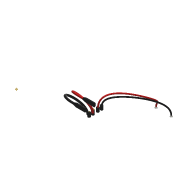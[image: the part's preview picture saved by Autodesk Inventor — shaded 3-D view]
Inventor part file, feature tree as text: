
AUTODESK INVENTOR PART (.ipt)
format: ipt  version: 2020 (Build 240168000, 168)  size: 544,256 bytes
history: native  units: in
note: dims shown in document units (in); Inventor stores cm internally (conversion verified against a paired STEP export)
features: other x18, reference x14, sketch x13, plane x10, sweep x6, pattern_linear x5, extrude x4, projected_geometry x4, loft x3
ambient origin geometry x8: Origin, YZ Plane, XZ Plane, XY Plane, X Axis, Y Axis, Z Axis, Center Point
bodies: Solid1 (feature_tree), Solid2 (feature_tree), Solid6 (feature_tree), Solid10 (feature_tree)
feature tree (77):
  sketch  "3D Sketch1"
  plane  "Work Plane1"
  extrude  "Extrusion1"  Depth=0.15in
  plane  "Work Plane2"
  loft  "Loft1"
  loft  "Loft2"
  sketch  "Sketch5"  dims[d11=0.06in d12=0.0in d13=90.0deg]
  sweep  "Sweep1"
  sweep  "Sweep2"
  plane  "Work Plane3"
  extrude  "Extrusion2"  Depth=0.05in
  plane  "Work Plane4"
  plane  "Work Plane5"
  sketch  "Sketch7"  dims[d18=0.0in d19=90.0deg d20=0.05in]
  plane  "Work Plane7"
  loft  "Loft3"
  pattern_linear  "Rectangular Pattern1"  Spacing1=0.1in  [1 undecoded]
  sketch  "Sketch9"  dims[d24=0.3937in d25=0.3937in]
  sweep  "Sweep3"
  sweep  "Sweep4"
  sketch  "3D Sketch2"
  plane  "Work Plane8"
  extrude  "Extrusion4"  Depth=0.03in
  plane  "Work Plane9"
  pattern_linear  "Rectangular Pattern3"  Spacing1=0.3937in  [1 undecoded]
  sketch  "Sketch13"  dims[d28=0.0in d29=0.0in]
  sweep  "Sweep6"
  sweep  "Sweep7"
  pattern_linear  "Rectangular Pattern4"  Spacing1=0.3937in  [1 undecoded]
  pattern_linear  "Rectangular Pattern5"  Count1=2 Spacing1=0.4in
  sketch  "Sketch14"  dims[d30=0.005in d31=0.1in d32=0.0in d37=0.175in d38=0.125in d39=0.03in d42=0.3937in d43=0.3937in d44=0.3937in d45=0.3937in d48=0.0in d49=90.0deg d50=0.3937in d51=90.0deg d52=0.7874in d54=0.4in d55=0.0in d56=0.0in d57=0.0in d58=0.0in d59=0.075in d60=0.07in d61=0.3937in d62=0.3937in d63=0.055in d64=0.03in d65=0.0in d75=6.2992in d77=0.1in d78=0.07in d79=0.05in d80=0.05in d81=0.0in d82=0.0in d83=0.0in d84=0.0in d85=0.7874in d87=1.5in d88=5.9055in d90=0.1in d91=0.025in d92=1.0in d93=0.0in d94=6.2992in d96=0.1in d97=0.0236in d98=0.0118in d100=0.0118in d101=0.0475in d102=0.0238in]
  plane  "Work Plane10"
  extrude  "Extrusion6"  TaperAngle=0.0deg  [1 undecoded]
  pattern_linear  "Rectangular Pattern6"  Spacing1=0.0in  [1 undecoded]
  other  "Work Point1"
  other  "Work Point2"
  other  "Work Point3"
  sketch  "Sketch1"  dims[d4=0.2in d5=0.15in]
  sketch  "Sketch2"  dims[d6=0.055in d7=0.0475in]
  other  "Edges1"
  sketch  "Sketch4"  dims[d8=0.2in d9=0.0in d10=0.0625in]
  other  "Edges2"
  projected_geometry  "Projected Loop1"
  projected_geometry  "Projected Loop2"
  sketch  "Sketch6"  dims[d14=0.0in d15=90.0deg d16=0.0in d17=90.0deg]
  reference  "Reference1"
  reference  "Reference2"
  reference  "Reference3"
  reference  "Reference4"
  plane  "Work Plane6"
  sketch  "Sketch8"  dims[d21=0.125in d22=0.3937in d23=0.3937in]
  reference  "Reference5"
  reference  "Reference6"
  projected_geometry  "Projected Loop3"
  projected_geometry  "Projected Loop4"
  other  "Work Point4"
  sketch  "Sketch10"  dims[d26=0.0in d27=0.0in]
  reference  "Reference7"
  reference  "Reference8"
  reference  "Reference9"
  reference  "Reference10"
  reference  "Reference11"
  reference  "Reference12"
  reference  "Reference13"
  reference  "Reference14"
  other  "<userpath>\Google Drive\Pirani Gauge\Pirani Gauge Modeling\Data Acquisition\Readout.iam"
  other  "Readout.iam"
  other  "Male Header - 1X2Wht:1"
  other  "Male Header - 1X2Wht:2"
  other  "MicroUSB Breakout:1"
  other  "pcb_microusb:1"
  other  "4x20 LCD:2"
  other  "16 pin header:1"
  other  "16 female pin:2"
  other  "Switch:1"
  other  "16 female pin:1"
  other  "PHS UNC2:11"
note: 5 required parameter values undecoded (feature->parameter linkage not recoverable at this tier; creation-order binding heuristic only, values carry confidence <= 0.55)
